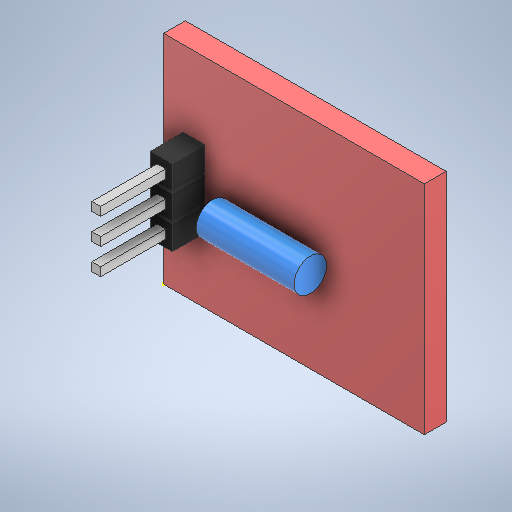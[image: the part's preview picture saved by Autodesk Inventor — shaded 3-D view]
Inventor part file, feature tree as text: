
AUTODESK INVENTOR PART (.ipt)
format: ipt  version: 2025.1 (Build 291241020, 241B)  size: 353,792 bytes
history: native  units: in
note: dims shown in document units (in); Inventor stores cm internally (conversion verified against a paired STEP export)
features: sketch x5, extrude x4, projected_geometry x3, plane x1
ambient origin geometry x8: Origin, YZ Plane, XZ Plane, XY Plane, X Axis, Y Axis, Z Axis, Center Point
bodies: Solid1 (feature_tree)
feature tree (13):
  extrude  "Extrusion1"  Depth=0.7874in
  plane  "Work Plane1"
  extrude  "Extrusion2"  [1 undecoded]
  sketch  "Sketch3"  dims[d5=0.1181in d6=0.3543in]
  extrude  "Extrusion3"  Depth=0.3543in
  extrude  "Extrusion5"  Depth=0.0787in
  sketch  "Sketch1"  dims[d0=0.9449in d1=0.7874in]
  sketch  "Sketch2"  dims[d2=0.0787in d3=0.0in d4=-0.3543in]
  sketch  "Sketch4"  dims[d7=0.3543in d8=0.0in d11=0.0787in d12=0.0866in]
  sketch  "Sketch6"  dims[d13=0.0787in d14=0.0866in d15=0.0787in d16=0.0866in d26=0.0079in d27=0.0079in d28=0.0709in d29=0.1181in d30=0.0in d45=0.0315in d46=0.0315in d47=0.0315in d48=0.0315in d49=0.0315in d50=0.0315in d51=0.2362in d52=0.0in d60=0.2756in]
  projected_geometry  "Projected Loop7"
  projected_geometry  "Projected Loop8"
  projected_geometry  "Projected Loop9"
note: 1 required parameter value undecoded (feature->parameter linkage not recoverable at this tier; creation-order binding heuristic only, values carry confidence <= 0.55)
